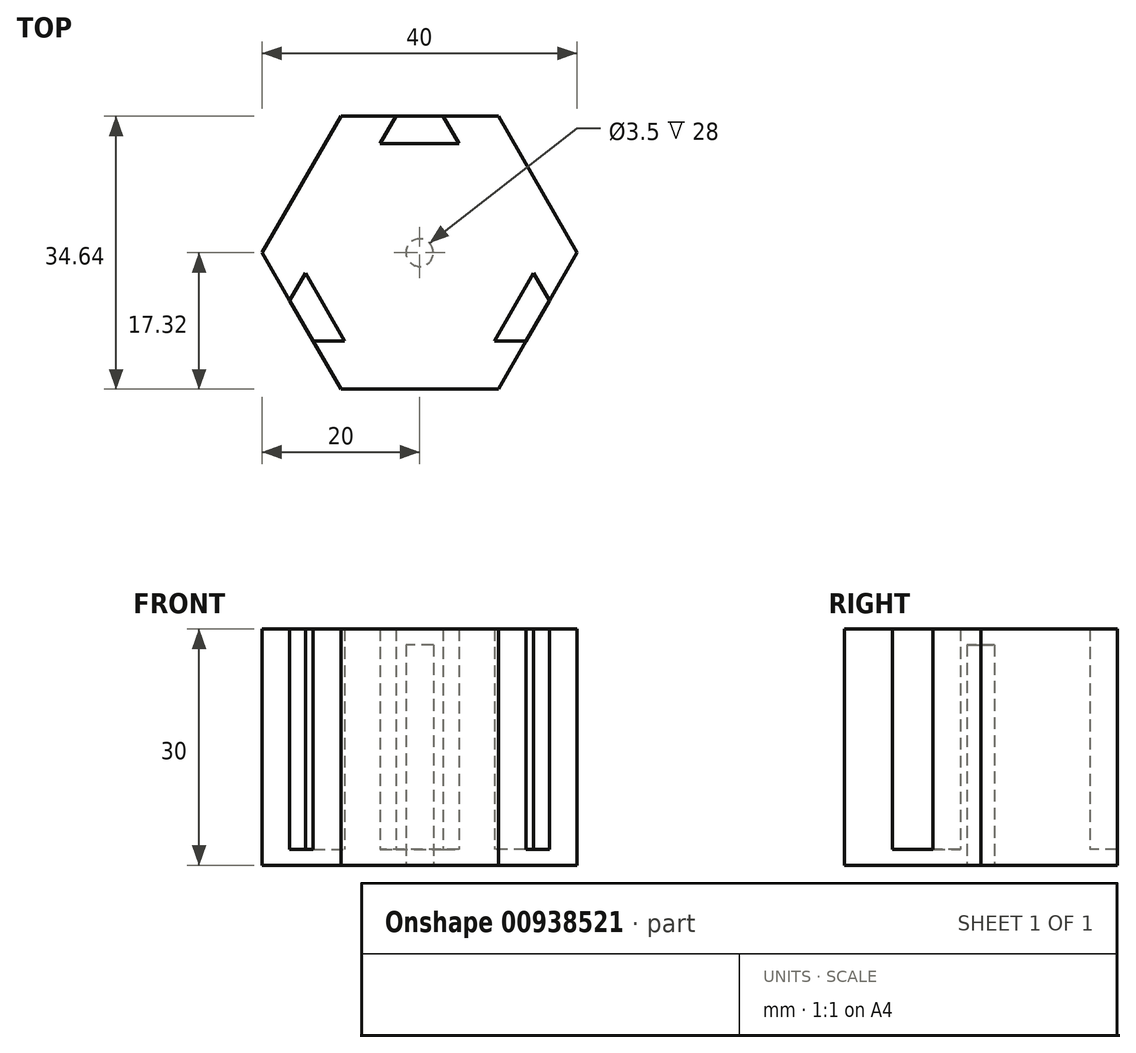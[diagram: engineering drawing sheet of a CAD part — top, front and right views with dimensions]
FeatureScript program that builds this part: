
annotation { "Feature Type Name" : "Feature", "Feature Type Description" : "" }
export const myFeature = defineFeature(function(context is Context, id is Id, definition is map)
    precondition{}
    {
        {
            var Q0;
            Q0=qCreatedBy(makeId("Top.planeOp"),FACE);
            var sketch = newSketch(context, id + "F0", { "sketchPlane" : qUnion([Q0])});
            skCircle(sketch, "E0.cCircle", {"center": v(0, 0) * mm, "radius": 20 * mm, "construction": true});
            skLineSegment(sketch, "E0.0", {"start": v(10, -17.32) * mm, "end": v(-10, -17.32) * mm});
            skLineSegment(sketch, "E0.1", {"start": v(-10, -17.32) * mm, "end": v(-20, 0) * mm});
            skLineSegment(sketch, "E0.2", {"start": v(-20, 0) * mm, "end": v(-10, 17.32) * mm});
            skLineSegment(sketch, "E0.3", {"start": v(-10, 17.32) * mm, "end": v(10, 17.32) * mm});
            skLineSegment(sketch, "E0.4", {"start": v(10, 17.32) * mm, "end": v(20, 0) * mm});
            skLineSegment(sketch, "E0.5", {"start": v(20, 0) * mm, "end": v(10, -17.32) * mm});
            skLineSegment(sketch, "E1", {"start": v(-3, 17.32) * mm, "end": v(3, 17.32) * mm});
            skLineSegment(sketch, "E2", {"start": v(3, 17.32) * mm, "end": v(5, 13.86) * mm});
            skLineSegment(sketch, "E3", {"start": v(5, 13.86) * mm, "end": v(-5, 13.86) * mm});
            skLineSegment(sketch, "E4", {"start": v(-5, 13.86) * mm, "end": v(-3, 17.32) * mm});
            skLineSegment(sketch, "E5.1.0", {"start": v(-16.5, -6.06) * mm, "end": v(-14.5, -2.6) * mm});
            skLineSegment(sketch, "E5.1.1", {"start": v(-9.5, -11.26) * mm, "end": v(-13.5, -11.26) * mm});
            skLineSegment(sketch, "E5.1.2", {"start": v(-14.5, -2.6) * mm, "end": v(-9.5, -11.26) * mm});
            skLineSegment(sketch, "E5.1.3", {"start": v(-13.5, -11.26) * mm, "end": v(-16.5, -6.06) * mm});
            skLineSegment(sketch, "E5.2.0", {"start": v(13.5, -11.26) * mm, "end": v(9.5, -11.26) * mm});
            skLineSegment(sketch, "E5.2.1", {"start": v(14.5, -2.6) * mm, "end": v(16.5, -6.06) * mm});
            skLineSegment(sketch, "E5.2.2", {"start": v(9.5, -11.26) * mm, "end": v(14.5, -2.6) * mm});
            skLineSegment(sketch, "E5.2.3", {"start": v(16.5, -6.06) * mm, "end": v(13.5, -11.26) * mm});
            skCircle(sketch, "E6", {"center": v(0, 0) * mm, "radius": 1.75 * mm});
            skSolve(sketch);
        }
        {
            var Q0;
            {var subQ3=sQuery(id+"F0.wireOp",EDGE,"E0.0");Q0=makeQuery(id+"F0.imprint","IMPRINT",FACE,{"disambiguationData":[TD([[makeQuery(id+"F0.imprint","IMPRINT",EDGE,{"derivedFrom":subQ3}),-1.0]])]});}
            extrude(context, id + "F1", {"entities" : qUnion([Q0]), "depth" : 30 * mm, "offsetDistance" : 25 * mm});
        }
        {
            var Q0;
            {var subQ0=sQuery(id+"F0.wireOp",EDGE,"E5.1.0");Q0=makeQuery(id+"F0.imprint","IMPRINT",FACE,{"disambiguationData":[TD([[makeQuery(id+"F0.imprint","IMPRINT",EDGE,{"derivedFrom":subQ0}),-1.0]])]});}
            var Q1;
            {var subQ0=sQuery(id+"F0.wireOp",EDGE,"E2");Q1=makeQuery(id+"F0.imprint","IMPRINT",FACE,{"disambiguationData":[TD([[makeQuery(id+"F0.imprint","IMPRINT",EDGE,{"derivedFrom":subQ0}),-1.0]])]});}
            var Q2;
            {var subQ0=sQuery(id+"F0.wireOp",EDGE,"E5.2.0");Q2=makeQuery(id+"F0.imprint","IMPRINT",FACE,{"disambiguationData":[TD([[makeQuery(id+"F0.imprint","IMPRINT",EDGE,{"derivedFrom":subQ0}),-1.0]])]});}
            extrude(context, id + "F2", {"entities" : qUnion([Q0, Q1, Q2]), "operationType" : NewBodyOperationType.ADD, "depth" : 2 * mm, "offsetDistance" : 25 * mm});
        }
        {
            var Q0;
            Q0=makeQuery(id+"F0.imprint","IMPRINT",FACE,{"disambiguationData":[TD([[makeQuery(id+"F0.imprint","IMPRINT",EDGE,{"derivedFrom":sQuery(id+"F0.wireOp",EDGE,"E6")}),1.0]])]});
            extrude(context, id + "F3", {"entities" : qUnion([Q0]), "operationType" : NewBodyOperationType.ADD, "depth" : 30 * mm, "offsetDistance" : 25 * mm, "hasSecondDirection" : true, "secondDirectionOppositeDirection" : false, "secondDirectionDepth" : 28 * mm});
        }
    });
